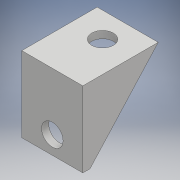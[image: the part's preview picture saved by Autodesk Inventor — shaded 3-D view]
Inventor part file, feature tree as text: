
AUTODESK INVENTOR PART (.ipt)
format: ipt  version: 2018.3 (Build 223284000, 284)  size: 128,000 bytes
history: native  units: mm
features: extrude x6, sketch x6, other x1
ambient origin geometry x8: Origin, YZ Plane, XZ Plane, XY Plane, X Axis, Y Axis, Z Axis, Center Point
bodies: Body1 (feature_tree)
feature tree (13):
  other  "Sólido1"
  extrude  "Extrusión1"  Depth=21.0mm
  extrude  "Extrusión3"  Depth=2.0mm TaperAngle=0.0deg
  extrude  "Extrusión5"  Depth=19.0mm TaperAngle=0.0deg
  extrude  "Extrusión6"  Depth=19.0mm TaperAngle=0.0deg
  extrude  "Extrusión7"  Depth=19.0mm TaperAngle=0.0deg
  extrude  "Extrusión8"  [1 undecoded]
  sketch  "Boceto2"  dims[d0=17.0mm d1=21.0mm]
  sketch  "Boceto3"  dims[d2=17.0mm d3=2.0mm d4=0.0mm]
  sketch  "Boceto5"  dims[d5=21.0mm d8=19.0mm d9=0.0mm]
  sketch  "Boceto6"  dims[d16=19.0mm d17=0.0mm d19=19.0mm d20=0.0mm]
  sketch  "Boceto7"  dims[d24=19.0mm d25=0.0mm d29=19.0mm d30=0.0mm]
  sketch  "Boceto8"
note: 1 required parameter value undecoded (feature->parameter linkage not recoverable at this tier; creation-order binding heuristic only, values carry confidence <= 0.55)
